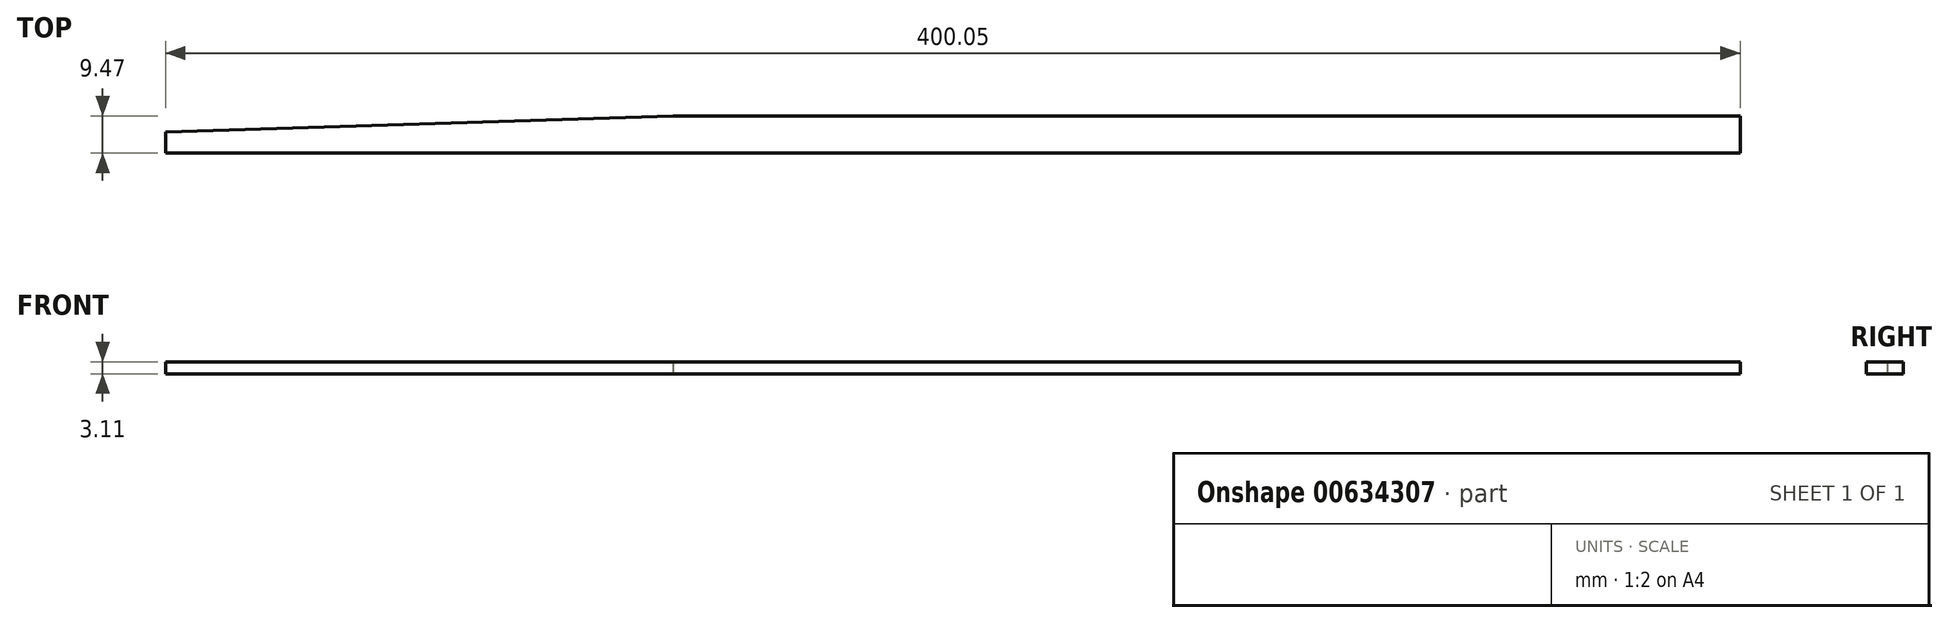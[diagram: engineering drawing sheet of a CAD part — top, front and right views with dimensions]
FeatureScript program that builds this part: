
annotation { "Feature Type Name" : "Feature", "Feature Type Description" : "" }
export const myFeature = defineFeature(function(context is Context, id is Id, definition is map)
    precondition{}
    {
        {
            var Q0;
            Q0=qCreatedBy(makeId("Top.planeOp"),FACE);
            var sketch = newSketch(context, id + "F0", { "sketchPlane" : qUnion([Q0])});
            skLineSegment(sketch, "E0", {"start": v(-28.87, 55.23) * mm, "end": v(371.18, 55.23) * mm});
            skLineSegment(sketch, "E1", {"start": v(371.18, 55.23) * mm, "end": v(371.18, 64.7) * mm});
            skLineSegment(sketch, "E2", {"start": v(-28.87, 55.23) * mm, "end": v(-28.87, 60.61) * mm});
            skLineSegment(sketch, "E3", {"start": v(371.18, 64.7) * mm, "end": v(100.08, 64.7) * mm});
            skLineSegment(sketch, "E4", {"start": v(-28.87, 60.61) * mm, "end": v(100.08, 64.7) * mm});
            skSolve(sketch);
        }
        {
            var Q0;
            Q0=makeQuery(id+"F0.imprint","IMPRINT",FACE,{"disambiguationData":[TD([[makeQuery(id+"F0.imprint","IMPRINT",EDGE,{"derivedFrom":sQuery(id+"F0.wireOp",EDGE,"E0")}),1.0]])]});
            extrude(context, id + "F1", {"entities" : qUnion([Q0]), "depth" : 3.1 * mm, "offsetDistance" : 25.4 * mm});
        }
    });
